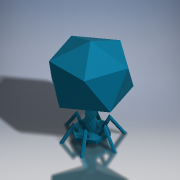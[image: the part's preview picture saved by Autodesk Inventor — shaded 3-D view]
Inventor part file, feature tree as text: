
AUTODESK INVENTOR PART (.ipt)
format: ipt  version: 2019 (Build 230136000, 136)  size: 1,128,448 bytes
history: native  units: in
note: dims shown in document units (in); Inventor stores cm internally (conversion verified against a paired STEP export)
features: split x31, plane x21, other x20, delete_face x11, sketch x10, extrude x10, loft x9, sweep x6, thicken_offset x5, surface_op x2
ambient origin geometry x8: Origin, YZ Plane, XZ Plane, XY Plane, X Axis, Y Axis, Z Axis, Center Point
bodies: Solid1 (feature_tree), Solid5 (feature_tree), Solid22 (feature_tree), Solid23 (feature_tree), Solid24 (feature_tree), Solid25 (feature_tree), Solid26 (feature_tree), Solid27 (feature_tree), Solid28 (feature_tree), Solid29 (feature_tree), Solid30 (feature_tree), Solid31 (feature_tree), Solid32 (feature_tree), Solid33 (feature_tree), Solid34 (feature_tree), Solid35 (feature_tree), Solid44 (feature_tree), Solid42 (feature_tree), Solid43 (feature_tree), Solid45 (feature_tree), Solid46 (feature_tree)
feature tree (125):
  plane  "Work Plane1"
  split  "Split1"
  thicken_offset  "Thicken3"
  thicken_offset  "Thicken4"
  thicken_offset  "Thicken5"
  delete_face  "Delete Face2"
  delete_face  "Delete Face3"
  delete_face  "Delete Face4"
  delete_face  "Delete Face5"
  delete_face  "Delete Face6"
  delete_face  "Delete Face7"
  delete_face  "Delete Face8"
  delete_face  "Delete Face9"
  surface_op  "Sculpt3"
  sketch  "Sketch6"  dims[d35=0.1181in d36=0.1181in]
  extrude  "Extrusion5"  Depth=0.1181in
  other  "Work Point14"
  other  "Work Point15"
  other  "Work Point16"
  other  "Work Point17"
  other  "Work Point18"
  other  "Work Point19"
  extrude  "Extrusion15"  Depth=0.1181in
  loft  "Loft15"
  extrude  "Extrusion16"  TaperAngle=0.0deg  [1 undecoded]
  loft  "Loft16"
  extrude  "Extrusion17"  TaperAngle=0.0deg  [1 undecoded]
  loft  "Loft17"
  extrude  "Extrusion18"  TaperAngle=0.0deg  [1 undecoded]
  loft  "Loft18"
  extrude  "Extrusion19"  Depth=1.9685in TaperAngle=0.0deg
  loft  "Loft19"
  extrude  "Extrusion20"  TaperAngle=0.0deg  [1 undecoded]
  loft  "Loft20"
  plane  "Work Plane23"
  plane  "Work Plane24"
  plane  "Work Plane25"
  plane  "Work Plane26"
  plane  "Work Plane27"
  plane  "Work Plane28"
  sketch  "Sketch7"  dims[d37=0.1181in d38=0.1181in]
  sweep  "Sweep1"
  sketch  "Sketch8"  dims[d39=0.1181in d40=0.1181in]
  sketch  "Sketch9"  dims[d41=0.1969in d42=0.0in]
  sweep  "Sweep2"
  sweep  "Sweep3"
  sketch  "Sketch10"  dims[d50=0.7874in d51=0.0in d123=4.7244in]
  sketch  "Sketch11"  dims[d124=1.1811in d125=0.0in d126=0.0in d127=90.0deg]
  sketch  "Sketch12"  dims[d128=0.0in d129=90.0deg d130=1.1811in d131=0.0in]
  sweep  "Sweep4"
  sweep  "Sweep5"
  sweep  "Sweep6"
  delete_face  "Delete Face10"
  delete_face  "Delete Face11"
  sketch  "Sketch13"  dims[d132=0.0in d133=90.0deg d134=0.0in d135=90.0deg]
  delete_face  "Delete Face12"
  extrude  "Extrusion21"  TaperAngle=120.0deg  [1 undecoded]
  other  "Work Point20"
  loft  "Loft21"
  plane  "Work Plane29"
  split  "Split20"
  extrude  "Extrusion22"  Depth=1.9685in
  plane  "Work Plane33"
  split  "Split24"
  loft  "Loft24"
  extrude  "Extrusion23"  Depth=1.9685in
  plane  "Work Plane34"
  split  "Split25"
  other  "Work Point22"
  loft  "Loft25"
  plane  "Work Plane35"
  plane  "Work Plane36"
  plane  "Work Plane37"
  plane  "Work Plane38"
  plane  "Work Plane39"
  plane  "Work Plane40"
  plane  "Work Plane41"
  plane  "Work Plane42"
  plane  "Work Plane43"
  plane  "Work Plane44"
  thicken_offset  "Thicken7"
  thicken_offset  "Thicken8"
  split  "Split26"
  split  "Split27"
  split  "Split28"
  split  "Split29"
  split  "Split30"
  split  "Split31"
  split  "Split32"
  split  "Split33"
  split  "Split34"
  split  "Split35"
  split  "Split36"
  split  "Split37"
  split  "Split38"
  split  "Split39"
  split  "Split40"
  split  "Split41"
  split  "Split42"
  split  "Split43"
  split  "Split44"
  split  "Split45"
  split  "Split46"
  plane  "Work Plane46"
  split  "Split47"
  split  "Split48"
  split  "Split49"
  split  "Split50"
  split  "Split51"
  split  "Split52"
  other  "Srf1"
  other  "Edges16"
  other  "Edges17"
  other  "Edges18"
  other  "Edges19"
  other  "Edges20"
  other  "Edges21"
  other  "Edges24"
  sketch  "Sketch14"  dims[d136=1.1811in d137=0.0in d138=0.0in d139=90.0deg]
  other  "Edges28"
  other  "Edges29"
  sketch  "Sketch15"  dims[d140=0.0in d141=90.0deg d142=1.1811in d143=0.0in d144=0.0in d145=90.0deg d146=0.0in d147=90.0deg d148=1.1811in d149=0.0in d150=0.0in d151=90.0deg d152=0.0in d153=90.0deg d154=1.1811in d155=0.0in d156=0.0in d157=90.0deg d158=0.0in d159=90.0deg d160=1.9685in d161=120.0deg d162=0.0in d163=0.0in d170=1.9685in d171=30.0deg d172=7.874in d173=0.4443in d176=7.874in d177=1.0147in d178=1.9685in d179=30.0deg d180=7.874in d181=0.4442in d182=0.0in d183=0.0in d184=0.0in d185=0.0in d186=1.9685in d187=120.0deg d188=7.874in d189=120.0deg d190=1.9685in d192=7.874in d193=0.4442in d194=120.0deg d197=1.9685in d198=150.0deg d199=7.874in d200=0.4442in d201=0.0in d202=0.0in d203=0.0in d204=0.0in d205=0.0in d206=0.0in d211=1.5748in d212=0.0in d213=0.0in d214=90.0deg d215=0.0in d216=90.0deg d217=0.3937in d222=7.0072in d223=0.0in d234=0.0in d235=90.0deg d236=0.0in d237=90.0deg d238=8.6614in d239=7.0072in d240=0.0in d241=0.0in d242=90.0deg d243=0.0in d244=90.0deg d245=1.9685in d246=1.9685in d247=1.9685in d248=1.9685in]
  other  "Edges30"
  other  "Scale2"
  surface_op  "Boundary Patch1"
note: 5 required parameter values undecoded (feature->parameter linkage not recoverable at this tier; creation-order binding heuristic only, values carry confidence <= 0.55)
